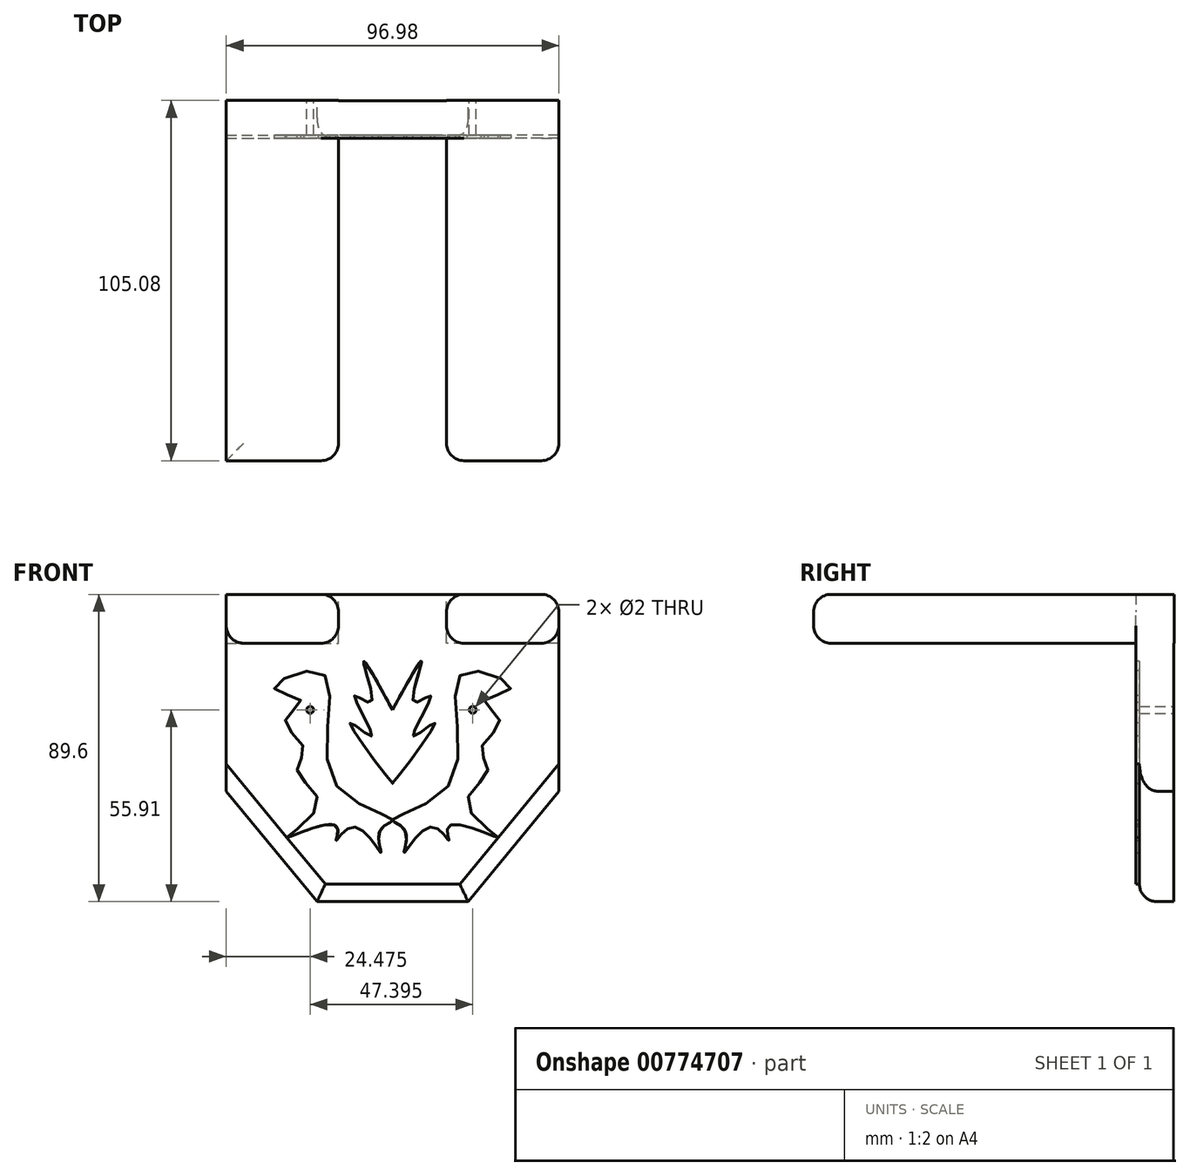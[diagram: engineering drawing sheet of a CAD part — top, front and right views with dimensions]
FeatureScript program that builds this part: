
annotation { "Feature Type Name" : "Feature", "Feature Type Description" : "" }
export const myFeature = defineFeature(function(context is Context, id is Id, definition is map)
    precondition{}
    {
        {
            var Q0;
            Q0=qCreatedBy(makeId("Front.planeOp"),FACE);
            var sketch = newSketch(context, id + "F0", { "sketchPlane" : qUnion([Q0])});
            skLineSegment(sketch, "E0", {"start": v(-48.5, 33.69) * mm, "end": v(48.5, 33.69) * mm});
            skLineSegment(sketch, "E1", {"start": v(48.5, 33.69) * mm, "end": v(48.5, -23.7) * mm});
            skLineSegment(sketch, "E2", {"start": v(48.5, -23.7) * mm, "end": v(22.03, -55.91) * mm});
            skLineSegment(sketch, "E3", {"start": v(22.03, -55.91) * mm, "end": v(0, -55.91) * mm});
            skLineSegment(sketch, "E4", {"start": v(0, 71.2) * mm, "end": v(0, -71.57) * mm, "construction": true});
            skLineSegment(sketch, "E5.MirrorCS", {"start": v(-48.5, 33.69) * mm, "end": v(-48.5, -23.7) * mm});
            skLineSegment(sketch, "E6.MirrorCS", {"start": v(-48.5, -23.7) * mm, "end": v(-22.03, -55.91) * mm});
            skLineSegment(sketch, "E7.MirrorCS", {"start": v(-22.03, -55.91) * mm, "end": v(0, -55.91) * mm});
            skLineSegment(sketch, "E8.bottom", {"start": v(-48.5, 19.43) * mm, "end": v(-15.74, 19.43) * mm});
            skLineSegment(sketch, "E8.top", {"start": v(-48.5, 33.69) * mm, "end": v(-15.74, 33.69) * mm});
            skLineSegment(sketch, "E8.left", {"start": v(-48.5, 19.43) * mm, "end": v(-48.5, 33.69) * mm});
            skLineSegment(sketch, "E8.right", {"start": v(-15.74, 19.43) * mm, "end": v(-15.74, 33.69) * mm});
            skLineSegment(sketch, "E9.MirrorCS", {"start": v(15.74, 19.43) * mm, "end": v(15.74, 33.69) * mm});
            skLineSegment(sketch, "E10.MirrorCS", {"start": v(48.5, 19.43) * mm, "end": v(15.74, 19.43) * mm});
            skSolve(sketch);
        }
        {
            var Q0;
            {var subQ3=sQuery(id+"F0.wireOp",EDGE,"E2");Q0=makeQuery(id+"F0.imprint","IMPRINT",FACE,{"disambiguationData":[TD([[makeQuery(id+"F0.imprint","IMPRINT",EDGE,{"derivedFrom":subQ3}),-1.0]])]});}
            extrude(context, id + "F1", {"entities" : qUnion([Q0]), "endBound" : BoundingType.SYMMETRIC, "depth" : 10 * mm, "offsetDistance" : 25.4 * mm});
        }
        {
            var Q0;
            Q0=makeQuery(id+"F0.imprint","IMPRINT",FACE,{"disambiguationData":[TD([[makeQuery(id+"F0.imprint","IMPRINT",EDGE,{"derivedFrom":sQuery(id+"F0.wireOp",EDGE,"E8.bottom")}),1.0]])]});
            var Q1;
            {var subQ3=sQuery(id+"F0.wireOp",EDGE,"E9.MirrorCS");Q1=makeQuery(id+"F0.imprint","IMPRINT",FACE,{"disambiguationData":[TD([[makeQuery(id+"F0.imprint","IMPRINT",EDGE,{"derivedFrom":subQ3}),-1.0]])]});}
            extrude(context, id + "F2", {"entities" : qUnion([Q0, Q1]), "operationType" : NewBodyOperationType.ADD, "depth" : 100 * mm, "offsetDistance" : 25.4 * mm, "hasSecondDirection" : true, "secondDirectionOppositeDirection" : true, "secondDirectionDepth" : 5.08 * mm});
        }
        {
            var Q0;
            Q0=makeQuery(id+"F2.opExtrude","SWEPT_EDGE",EDGE,{"disambiguationData":[OSD([sQuery(id+"F0.wireOp",EDGE,"E8.top"),sQuery(id+"F0.wireOp",EDGE,"E8.left")])]});
            var Q1;
            {var subQ0=sQuery(id+"F0.wireOp",EDGE,"E8.bottom");var subQ1=sQuery(id+"F0.wireOp",EDGE,"E5.MirrorCS");var subQ2=sQuery(id+"F0.wireOp",EDGE,"E8.right");var subQ3=sQuery(id+"F0.wireOp",EDGE,"E8.left");Q1=makeQuery(id+"F2.boolean.opBoolean","SPLIT",EDGE,{"disambiguationData":[TD([makeQuery(id+"F2.opExtrude","CAP_FACE",FACE,{"disambiguationData":[OSD([subQ0,sQuery(id+"F0.wireOp",EDGE,"E8.top"),subQ3,subQ2])],"isStart":false})])],"derivedFrom":makeQuery(id+"F2.opExtrude","SWEPT_EDGE",EDGE,{"disambiguationData":[OSD([subQ1,subQ0,subQ3])]})});}
            var Q2;
            {var subQ0=sQuery(id+"F0.wireOp",EDGE,"E0");var subQ1=sQuery(id+"F0.wireOp",EDGE,"E8.right");var subQ2=sQuery(id+"F0.wireOp",EDGE,"E8.top");var subQ3=sQuery(id+"F0.wireOp",EDGE,"E8.bottom");Q2=makeQuery(id+"F2.boolean.opBoolean","SPLIT",EDGE,{"disambiguationData":[TD([makeQuery(id+"F2.opExtrude","CAP_FACE",FACE,{"disambiguationData":[OSD([subQ3,subQ2,sQuery(id+"F0.wireOp",EDGE,"E8.left"),subQ1])],"isStart":false})])],"derivedFrom":makeQuery(id+"F2.opExtrude","SWEPT_EDGE",EDGE,{"disambiguationData":[OSD([subQ0,subQ2,subQ1])]})});}
            var Q3;
            Q3=makeQuery(id+"F2.opExtrude","CAP_EDGE",EDGE,{"disambiguationData":[OSD([sQuery(id+"F0.wireOp",EDGE,"E8.right")])],"isStart":false});
            var Q4;
            Q4=makeQuery(id+"F2.opExtrude","CAP_EDGE",EDGE,{"disambiguationData":[OSD([sQuery(id+"F0.wireOp",EDGE,"E8.top")])],"isStart":false});
            var Q5;
            Q5=makeQuery(id+"F2.opExtrude","CAP_EDGE",EDGE,{"disambiguationData":[OSD([sQuery(id+"F0.wireOp",EDGE,"E8.bottom")])],"isStart":false});
            var Q6;
            Q6=makeQuery(id+"F2.opExtrude","CAP_EDGE",EDGE,{"disambiguationData":[OSD([sQuery(id+"F0.wireOp",EDGE,"E8.left")])],"isStart":false});
            var Q7;
            {var subQ0=sQuery(id+"F0.wireOp",EDGE,"E8.right");var subQ1=sQuery(id+"F0.wireOp",EDGE,"E8.bottom");Q7=makeQuery(id+"F2.boolean.opBoolean","SPLIT",EDGE,{"disambiguationData":[TD([makeQuery(id+"F2.opExtrude","CAP_FACE",FACE,{"disambiguationData":[OSD([subQ1,sQuery(id+"F0.wireOp",EDGE,"E8.top"),sQuery(id+"F0.wireOp",EDGE,"E8.left"),subQ0])],"isStart":false})])],"derivedFrom":makeQuery(id+"F2.opExtrude","SWEPT_EDGE",EDGE,{"disambiguationData":[OSD([subQ1,subQ0])]})});}
            var Q8;
            Q8=makeQuery(id+"F1.opExtrude","CAP_EDGE",EDGE,{"disambiguationData":[OSD([sQuery(id+"F0.wireOp",EDGE,"E8.right")])],"isStart":false});
            var Q9;
            {var subQ0=sQuery(id+"F0.wireOp",EDGE,"E10.MirrorCS");var subQ1=sQuery(id+"F0.wireOp",EDGE,"E9.MirrorCS");var subQ2=sQuery(id+"F0.wireOp",EDGE,"E1");var subQ3=sQuery(id+"F0.wireOp",EDGE,"E0");Q9=makeQuery(id+"F2.boolean.opBoolean","SPLIT",EDGE,{"disambiguationData":[TD([makeQuery(id+"F2.opExtrude","CAP_FACE",FACE,{"disambiguationData":[OSD([subQ3,subQ2,subQ1,subQ0])],"isStart":false})])],"derivedFrom":makeQuery(id+"F2.opExtrude","SWEPT_EDGE",EDGE,{"disambiguationData":[OSD([subQ3,subQ1])]})});}
            var Q10;
            {var subQ0=sQuery(id+"F0.wireOp",EDGE,"E10.MirrorCS");var subQ1=sQuery(id+"F0.wireOp",EDGE,"E9.MirrorCS");var subQ2=sQuery(id+"F0.wireOp",EDGE,"E1");var subQ3=sQuery(id+"F0.wireOp",EDGE,"E0");Q10=makeQuery(id+"F2.boolean.opBoolean","SPLIT",EDGE,{"disambiguationData":[TD([makeQuery(id+"F2.opExtrude","CAP_FACE",FACE,{"disambiguationData":[OSD([subQ3,subQ2,subQ1,subQ0])],"isStart":false})])],"derivedFrom":makeQuery(id+"F2.opExtrude","SWEPT_EDGE",EDGE,{"disambiguationData":[OSD([subQ1,subQ0])]})});}
            var Q11;
            Q11=makeQuery(id+"F1.opExtrude","CAP_EDGE",EDGE,{"disambiguationData":[OSD([sQuery(id+"F0.wireOp",EDGE,"E9.MirrorCS")])],"isStart":false});
            var Q12;
            Q12=makeQuery(id+"F2.opExtrude","CAP_EDGE",EDGE,{"disambiguationData":[OSD([sQuery(id+"F0.wireOp",EDGE,"E10.MirrorCS")])],"isStart":false});
            var Q13;
            Q13=makeQuery(id+"F2.opExtrude","CAP_EDGE",EDGE,{"disambiguationData":[OSD([sQuery(id+"F0.wireOp",EDGE,"E9.MirrorCS")])],"isStart":false});
            var Q14;
            Q14=makeQuery(id+"F2.opExtrude","CAP_EDGE",EDGE,{"disambiguationData":[OSD([sQuery(id+"F0.wireOp",EDGE,"E0")])],"isStart":false});
            var Q15;
            Q15=makeQuery(id+"F2.opExtrude","CAP_EDGE",EDGE,{"disambiguationData":[OSD([sQuery(id+"F0.wireOp",EDGE,"E1")])],"isStart":false});
            var Q16;
            Q16=makeQuery(id+"F2.opExtrude","SWEPT_EDGE",EDGE,{"disambiguationData":[OSD([sQuery(id+"F0.wireOp",EDGE,"E0"),sQuery(id+"F0.wireOp",EDGE,"E1")])]});
            var Q17;
            {var subQ0=sQuery(id+"F0.wireOp",EDGE,"E1");var subQ1=sQuery(id+"F0.wireOp",EDGE,"E10.MirrorCS");var subQ2=sQuery(id+"F0.wireOp",EDGE,"E9.MirrorCS");var subQ3=sQuery(id+"F0.wireOp",EDGE,"E0");Q17=makeQuery(id+"F2.boolean.opBoolean","SPLIT",EDGE,{"disambiguationData":[TD([makeQuery(id+"F2.opExtrude","CAP_FACE",FACE,{"disambiguationData":[OSD([subQ3,subQ0,subQ2,subQ1])],"isStart":false})])],"derivedFrom":makeQuery(id+"F2.opExtrude","SWEPT_EDGE",EDGE,{"disambiguationData":[OSD([subQ0,subQ1])]})});}
            var Q18;
            Q18=makeQuery(id+"F1.opExtrude","CAP_EDGE",EDGE,{"disambiguationData":[OSD([sQuery(id+"F0.wireOp",EDGE,"E2")])],"isStart":false});
            var Q19;
            Q19=makeQuery(id+"F1.opExtrude","CAP_EDGE",EDGE,{"disambiguationData":[OSD([sQuery(id+"F0.wireOp",EDGE,"E3"),sQuery(id+"F0.wireOp",EDGE,"E7.MirrorCS")])],"isStart":false});
            var Q20;
            Q20=makeQuery(id+"F1.opExtrude","CAP_EDGE",EDGE,{"disambiguationData":[OSD([sQuery(id+"F0.wireOp",EDGE,"E6.MirrorCS")])],"isStart":false});
            fillet(context, id + "F3", {"entities" : qUnion([Q0, Q1, Q2, Q3, Q4, Q5, Q6, Q7, Q8, Q9, Q10, Q11, Q12, Q13, Q14, Q15, Q16, Q17, Q18, Q19, Q20]), "radius" : 5.08 * mm, "tangentPropagation" : true, "allowEdgeOverflow" : false});
        }
        {
            var Q0;
            Q0=makeQuery(id+"F1.opExtrude","CAP_FACE",FACE,{"disambiguationData":[OSD([sQuery(id+"F0.wireOp",EDGE,"E0"),sQuery(id+"F0.wireOp",EDGE,"E1"),sQuery(id+"F0.wireOp",EDGE,"E2"),sQuery(id+"F0.wireOp",EDGE,"E3"),sQuery(id+"F0.wireOp",EDGE,"E5.MirrorCS"),sQuery(id+"F0.wireOp",EDGE,"E6.MirrorCS"),sQuery(id+"F0.wireOp",EDGE,"E7.MirrorCS"),sQuery(id+"F0.wireOp",EDGE,"E8.bottom"),sQuery(id+"F0.wireOp",EDGE,"E8.right"),sQuery(id+"F0.wireOp",EDGE,"E9.MirrorCS"),sQuery(id+"F0.wireOp",EDGE,"E10.MirrorCS")])],"isStart":false});
            var sketch = newSketch(context, id + "F4", { "sketchPlane" : qUnion([Q0])});
            skFitSpline(sketch, "E11", {"points": [v(0, 0) * mm, v(-8.38, 14.17) * mm, v(-6.24, 2.22) * mm, v(-11.1, 4.12) * mm, v(-6.07, -7.62) * mm, v(-12.3, -3.84) * mm, v(0, -21.41) * mm, v(-3.13, -13.15) * mm, v(0, -8.84) * mm, v(-2.74, -4.55) * mm, v(0, 0) * mm, v(0, 0) * mm]});
            skFitSpline(sketch, "E12", {"points": [v(-20.62, 10.77) * mm, v(-17.32, -20.6) * mm, v(0, -32.05) * mm, v(-3.76, -35.48) * mm, v(-3.36, -41.75) * mm, v(-11.32, -34.1) * mm, v(-16.47, -38.23) * mm, v(-16.5, -33.79) * mm, v(-30.82, -37.21) * mm, v(-21.73, -27.69) * mm, v(-27.77, -17.84) * mm, v(-25.87, -11.2) * mm, v(-31.26, -2.91) * mm, v(-26.7, 2.74) * mm, v(-34.47, 6.29) * mm, v(-20.62, 10.77) * mm]});
            skFitSpline(sketch, "E13.MirrorC", {"points": [v(0, 0) * mm, v(8.38, 14.17) * mm, v(6.24, 2.22) * mm, v(11.1, 4.12) * mm, v(6.07, -7.62) * mm, v(12.3, -3.84) * mm, v(0, -21.41) * mm, v(3.13, -13.15) * mm, v(0, -8.84) * mm, v(2.74, -4.55) * mm, v(0, 0) * mm, v(0, 0) * mm]});
            skFitSpline(sketch, "E14.MirrorC", {"points": [v(20.62, 10.77) * mm, v(17.32, -20.6) * mm, v(0, -32.05) * mm, v(3.76, -35.48) * mm, v(3.36, -41.75) * mm, v(11.32, -34.1) * mm, v(16.47, -38.23) * mm, v(16.5, -33.79) * mm, v(30.82, -37.21) * mm, v(21.73, -27.69) * mm, v(27.77, -17.84) * mm, v(25.87, -11.2) * mm, v(31.26, -2.91) * mm, v(26.7, 2.74) * mm, v(34.47, 6.29) * mm, v(20.62, 10.77) * mm]});
            skSolve(sketch);
        }
        {
            var Q0;
            {var subQ11=sQuery(id+"F4.wireOp",EDGE,"E13.MirrorC");var subQ12=sQuery(id+"F4.wireOp",EDGE,"E11");var subQ16=makeQuery(id+"F4.imprint","INTERSECT",VERTEX,{"disambiguationData":[OD(0.0)],"derivedFrom":[subQ12,subQ11]});Q0=makeQuery(id+"F4.imprint","IMPRINT",FACE,{"disambiguationData":[TD([[makeQuery(id+"F4.imprint","IMPRINT",EDGE,{"disambiguationData":[TD([[subQ16,1.0]])],"derivedFrom":subQ12}),-1.0]])]});}
            var Q1;
            {var subQ0=sQuery(id+"F0.wireOp",EDGE,"E7.MirrorCS");var subQ1=sQuery(id+"F0.wireOp",EDGE,"E6.MirrorCS");var subQ2=sQuery(id+"F0.wireOp",EDGE,"E3");var subQ3=sQuery(id+"F0.wireOp",EDGE,"E2");var subQ4=makeQuery(id+"F1.opExtrude","CAP_FACE",FACE,{"disambiguationData":[OSD([sQuery(id+"F0.wireOp",EDGE,"E0"),sQuery(id+"F0.wireOp",EDGE,"E1"),subQ3,subQ2,sQuery(id+"F0.wireOp",EDGE,"E5.MirrorCS"),subQ1,subQ0,sQuery(id+"F0.wireOp",EDGE,"E8.bottom"),sQuery(id+"F0.wireOp",EDGE,"E8.right"),sQuery(id+"F0.wireOp",EDGE,"E9.MirrorCS"),sQuery(id+"F0.wireOp",EDGE,"E10.MirrorCS")])],"isStart":false});var subQ5=makeQuery(id+"F3.opFillet","BLEND_EDGE",EDGE,{"blendedFrom":[makeQuery(id+"F1.opExtrude","CAP_EDGE",EDGE,{"disambiguationData":[OSD([subQ2,subQ0])],"isStart":false}),subQ4],"blendedInto":[subQ4]});Q1=makeQuery(id+"F4.imprint","IMPRINT",FACE,{"disambiguationData":[TD([[makeQuery(id+"F4.imprint","IMPRINT",EDGE,{"derivedFrom":subQ5}),1.0]])]});}
            extrude(context, id + "F5", {"entities" : qUnion([Q0, Q1]), "operationType" : NewBodyOperationType.ADD, "depth" : 1 * mm, "offsetDistance" : 25.4 * mm});
        }
        {
            var Q0;
            Q0=makeQuery(id+"F1.opExtrude","CAP_FACE",FACE,{"disambiguationData":[OSD([sQuery(id+"F0.wireOp",EDGE,"E0"),sQuery(id+"F0.wireOp",EDGE,"E1"),sQuery(id+"F0.wireOp",EDGE,"E2"),sQuery(id+"F0.wireOp",EDGE,"E3"),sQuery(id+"F0.wireOp",EDGE,"E5.MirrorCS"),sQuery(id+"F0.wireOp",EDGE,"E6.MirrorCS"),sQuery(id+"F0.wireOp",EDGE,"E7.MirrorCS"),sQuery(id+"F0.wireOp",EDGE,"E8.bottom"),sQuery(id+"F0.wireOp",EDGE,"E8.right"),sQuery(id+"F0.wireOp",EDGE,"E9.MirrorCS"),sQuery(id+"F0.wireOp",EDGE,"E10.MirrorCS")])],"isStart":true});
            var sketch = newSketch(context, id + "F6", { "sketchPlane" : qUnion([Q0])});
            skLineSegment(sketch, "E15", {"start": v(-23.38, 0) * mm, "end": v(24.01, 0) * mm, "construction": true});
            skCircle(sketch, "E16", {"center": v(-23.38, 0) * mm, "radius": 1 * mm});
            skCircle(sketch, "E17", {"center": v(24.01, 0) * mm, "radius": 1 * mm});
            skSolve(sketch);
        }
        {
            var Q0;
            Q0=sQuery(id+"F6.wireOp",VERTEX,"E15.end");
            var Q1;
            Q1=sQuery(id+"F6.wireOp",VERTEX,"E15.start");
            var Q2;
            Q2=makeQuery(id+"F1.opExtrude","SWEPT_BODY",BODY,{"disambiguationData":[OSD([sQuery(id+"F0.wireOp",EDGE,"E0"),sQuery(id+"F0.wireOp",EDGE,"E1"),sQuery(id+"F0.wireOp",EDGE,"E2"),sQuery(id+"F0.wireOp",EDGE,"E3"),sQuery(id+"F0.wireOp",EDGE,"E5.MirrorCS"),sQuery(id+"F0.wireOp",EDGE,"E6.MirrorCS"),sQuery(id+"F0.wireOp",EDGE,"E7.MirrorCS"),sQuery(id+"F0.wireOp",EDGE,"E8.bottom"),sQuery(id+"F0.wireOp",EDGE,"E8.right"),sQuery(id+"F0.wireOp",EDGE,"E9.MirrorCS"),sQuery(id+"F0.wireOp",EDGE,"E10.MirrorCS")])]});
            hole(context, id + "F7", {"style" : HoleStyle.SIMPLE, "endStyle" : HoleEndStyle.THROUGH, "holeDiameter" : 2 * mm, "majorDiameter" : 6.35 * mm, "isTappedThrough" : true, "tappedDepth" : 12.7 * mm, "tapClearance" : 3, "locations" : qUnion([Q0, Q1]), "scope" : qUnion([Q2])});
        }
    });
